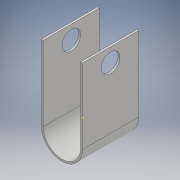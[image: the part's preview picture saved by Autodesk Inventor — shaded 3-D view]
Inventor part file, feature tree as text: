
AUTODESK INVENTOR PART (.ipt)
format: ipt  version: 2018 (Build 220112000, 112)  size: 118,272 bytes
history: native  units: mm
features: sketch x4, extrude x2, projected_geometry x1
ambient origin geometry x8: Origin, YZ Plane, XZ Plane, XY Plane, X Axis, Y Axis, Z Axis, Center Point
bodies: Solid1 (feature_tree)
feature tree (7):
  extrude  "Extrusion1"  Depth=20.0mm
  sketch  "Sketch2"  dims[d2=30.0mm d3=0.0mm d4=10.0mm]
  sketch  "Sketch3"  dims[d5=10.0mm d6=0.0mm]
  extrude  "Extrusion2"  Depth=10.0mm
  sketch  "Sketch1"  dims[d0=22.0mm d1=20.0mm]
  sketch  "Sketch4"  dims[d7=40.0mm d8=40.0mm]
  projected_geometry  "Projected Loop1"
